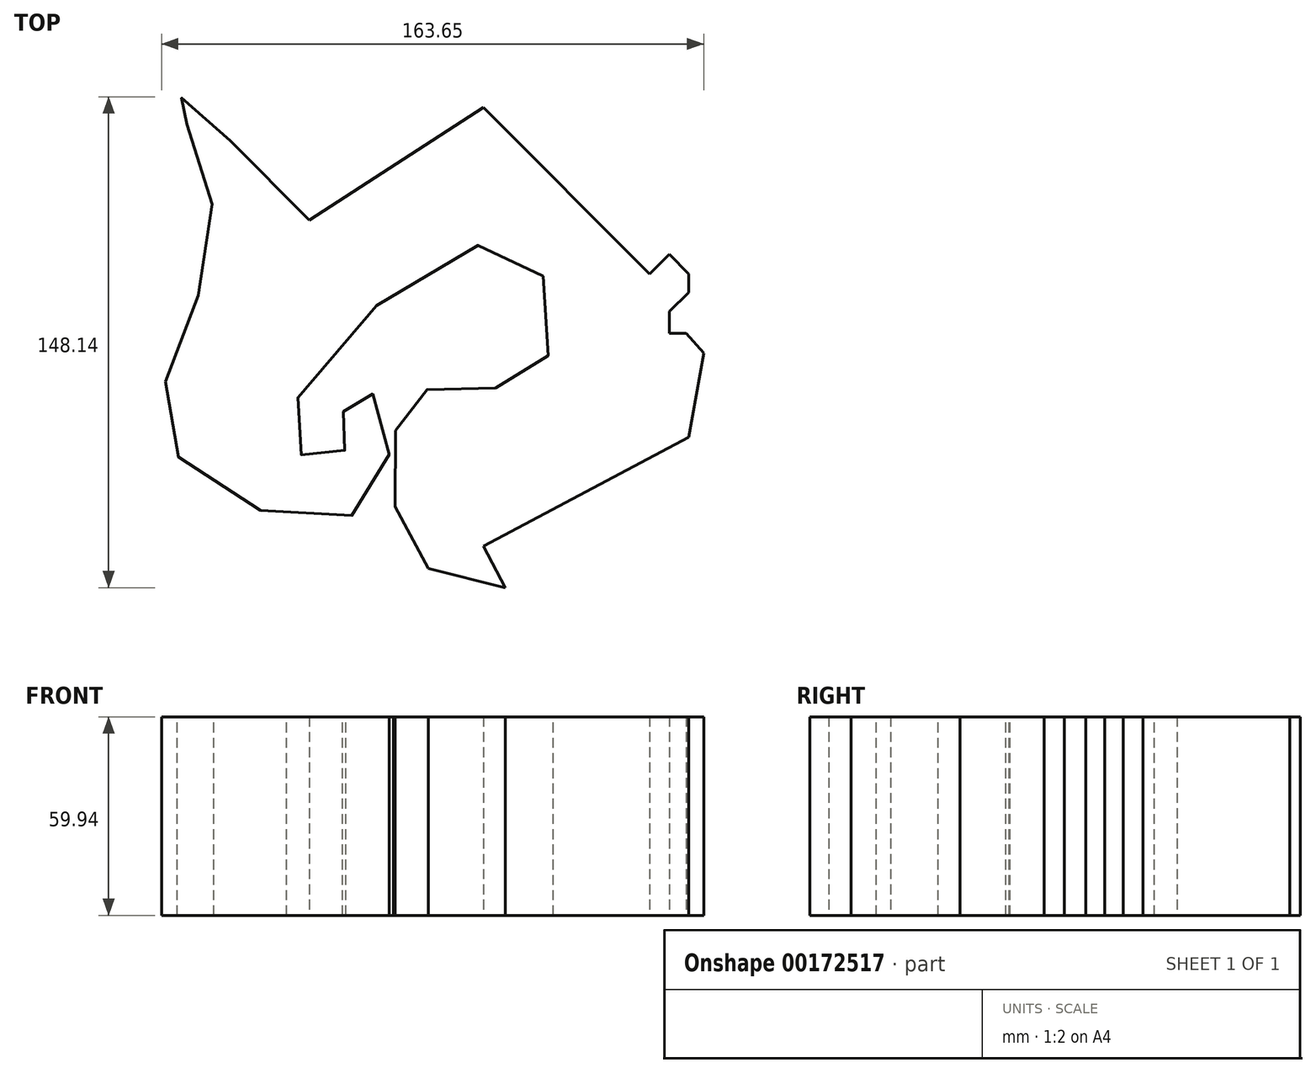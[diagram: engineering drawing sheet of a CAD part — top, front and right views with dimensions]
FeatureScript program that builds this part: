
annotation { "Feature Type Name" : "Feature", "Feature Type Description" : "" }
export const myFeature = defineFeature(function(context is Context, id is Id, definition is map)
    precondition{}
    {
        {
            var Q0;
            Q0=qCreatedBy(makeId("Top.planeOp"),FACE);
            var sketch = newSketch(context, id + "F0", { "sketchPlane" : qUnion([Q0])});
            skLineSegment(sketch, "E0", {"start": v(-47.43, 21.86) * mm, "end": v(5.12, 55.9) * mm});
            skLineSegment(sketch, "E1", {"start": v(5.12, 55.9) * mm, "end": v(55.26, 5.62) * mm});
            skLineSegment(sketch, "E2", {"start": v(55.26, 5.62) * mm, "end": v(61.23, 11.57) * mm});
            skLineSegment(sketch, "E3", {"start": v(61.23, 11.57) * mm, "end": v(67.16, 5.62) * mm});
            skLineSegment(sketch, "E4", {"start": v(67.16, 5.62) * mm, "end": v(67.16, 0) * mm});
            skLineSegment(sketch, "E5", {"start": v(67.16, 0) * mm, "end": v(61.23, -5.65) * mm});
            skLineSegment(sketch, "E6", {"start": v(61.23, -5.65) * mm, "end": v(61.23, -12.26) * mm});
            skLineSegment(sketch, "E7", {"start": v(61.23, -12.26) * mm, "end": v(66.34, -12.26) * mm});
            skLineSegment(sketch, "E8", {"start": v(66.34, -12.26) * mm, "end": v(71.64, -18.26) * mm});
            skLineSegment(sketch, "E9", {"start": v(71.64, -18.26) * mm, "end": v(67.16, -43.65) * mm});
            skLineSegment(sketch, "E10", {"start": v(67.16, -43.65) * mm, "end": v(5.12, -76.54) * mm});
            skLineSegment(sketch, "E11", {"start": v(5.12, -76.54) * mm, "end": v(11.77, -89.09) * mm});
            skLineSegment(sketch, "E12", {"start": v(11.77, -89.09) * mm, "end": v(-11.52, -83.3) * mm});
            skLineSegment(sketch, "E13", {"start": v(-11.52, -83.3) * mm, "end": v(-21.55, -64.65) * mm});
            skFitSpline(sketch, "E14", {"points": [v(-21.55, -64.65) * mm, v(-14.42, -30.17) * mm, v(21.7, -24.13) * mm, v(11.9, 14.65) * mm, v(-54.1, -44.2) * mm, v(-37.45, -48.65) * mm, v(-37.3, -36.72) * mm, v(-28.78, -30.32) * mm, v(-29.99, -64.65) * mm, v(-89.97, -44.9) * mm, v(-76.3, 19.27) * mm, v(-87.29, 58.84) * mm, v(-47.43, 21.86) * mm], "startDerivative": vector(-31.52, 568.31) * mm, "endDerivative": vector(583.74, -596.14) * mm});
            skSolve(sketch);
        }
        {
            var Q0;
            Q0 = qSketchRegion(id + "F0", true);
            extrude(context, id + "F1", {"entities" : qUnion([Q0]), "depth" : 59.94 * mm});
        }
    });
